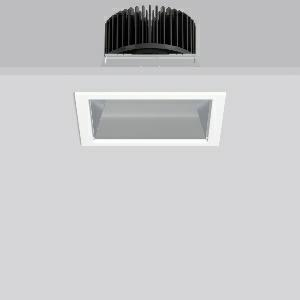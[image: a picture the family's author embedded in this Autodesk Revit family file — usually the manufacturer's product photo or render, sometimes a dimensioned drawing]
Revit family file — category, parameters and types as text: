
# Revit family: quardo_901705_002_f566
name_source: partatom
category: Lighting Fixtures
units: mm (PartAtom-declared; Revit-internal decimal feet)

## family parameters
Cut with Voids When Loaded = No
Host = Face
Light Source = No
Part Type = Normal
Room Calculation Point = No
Round Connector Dimension = Use Diameter
Shared = No

## types (1)
- QUARDO (1 x LED Modul 830, 2500 lm, 3000)
    Apparent Load = 19 VA
    CIE Flux Codes = 80 100 100 100 100
    Color Rendering = 80
    Color Temperature = 3000
    Default Elevation = 1800 mm
    Description = Series: QUARDO
High-quality recessed downlight with square luminous surface. Recessed mounting frame: die-cast aluminium, powder-coated. Mounting bracket: galvanised sheet steel. Reflector: aluminium, highly polished anodised finish. Ceiling installation with spring system. Including separate LED converter with connecting cable 600 mm. Through-wiring box (5 pole) available as accessory. 
Colour: traffic white, matt (RAL 9016)
Length: 176 mm
Width: 176 mm
Height: 4 mm
Cut-out length: 165 mm
Cut-out width: 165 mm
Recess height: 150 mm
Luminaire: recess height: 145 mm
Lamp: LED
Socket: without socket
Colour temperature: 3000K
Colour rendering index (CRI): 85
System power: 19 W
Rated luminous flux: 2500 lm
Luminous efficiency: 132 lm/W
Control gear: Regulated power supply
Protection class: II
Type of protection: IP 20
    Height = 0 mm  [stored 0 ft]
    Lamp = 1 x LED Modul 830
    Lamp Light Flux = 2500 lm
    Lamp count = 1
    Length = 176 mm
    Lifetime = 50000 h
    Luminous efficacy = 132 lm/W
    Manufacturer = RZB
    ModVariant = No
    Model = 901705.002
    Mounting Place = Ceiling
    Mounting Type = Recessed
    Number of Poles = 1
    OnlyDefault = Yes
    Power Factor = 1
    Product Name = QUARDO
    Product group = Recessed downlights
    ProductGroupID = 402
    Protection Class = Protection class II
    Protection Degree = IP 20
    RLX_Detail_Level = 1
    RLX_Emergency_Light_Flux = 0 lm
    RLX_Emergency_Type = 0
    RLX_Emergency_Type_DB = No
    RlxData = <blob elided: 29277 chars, md5=f9ffec6e>
    Socket = socket
    Standby Power = 0 W
    System Light Flux = 2500 lm
    System Power = 19 W
    Type Comments = Product without accessories
    Type Image = 901705.002.jpg
    URL = http://relux.com
    VarID = ---
    Voltage = 230 V
    Voltage Range = 220-240 V
    Weight = 0.00 kg
    Width = 176 mm

note: [stored X ft] marks values corroborated as IEEE doubles in the binary element streams (Revit-internal decimal feet)

## geometry (parser evidence)
native form markers: Blend x4, Sweep x9
no freeform markers — native parametric forms only
